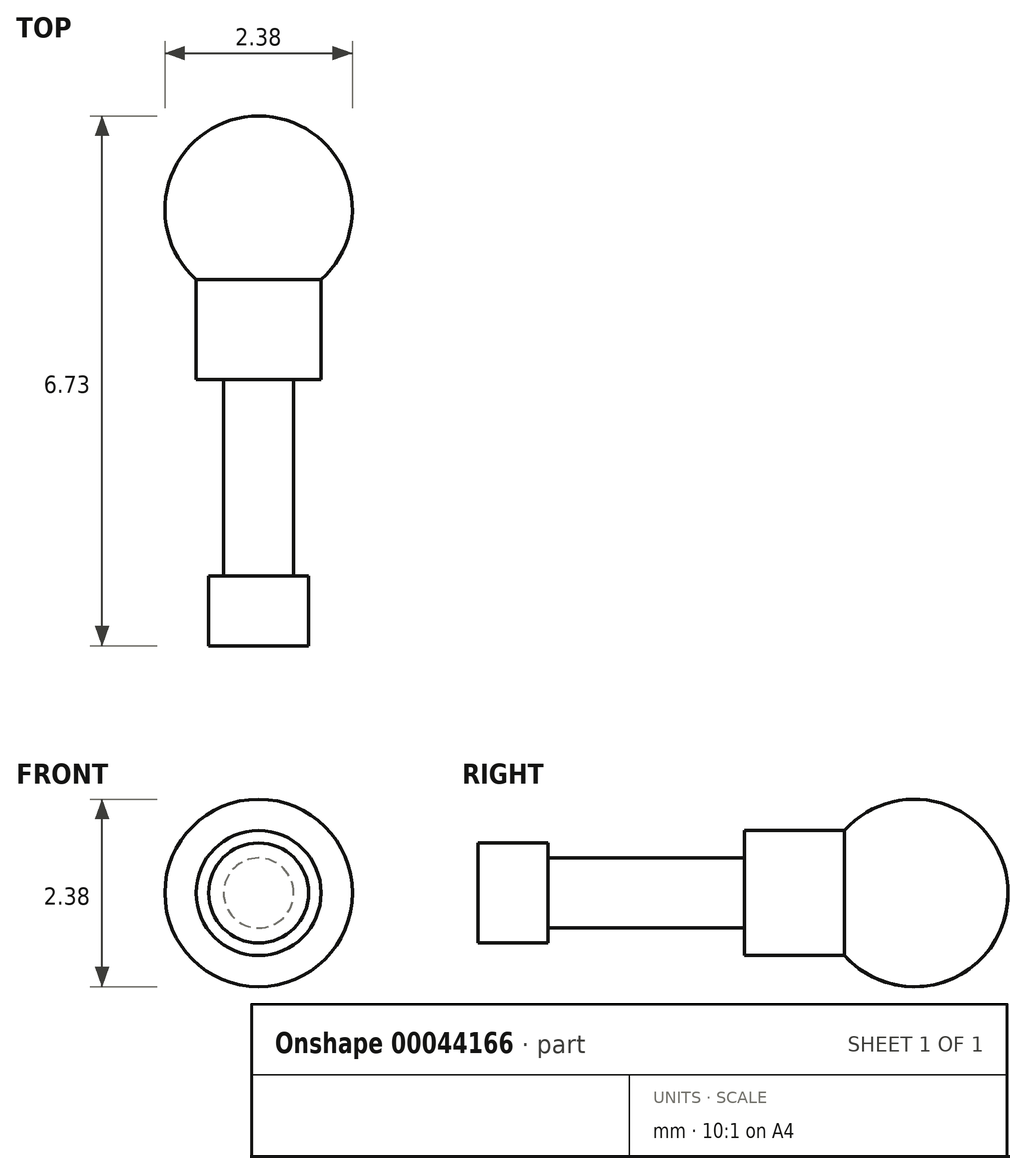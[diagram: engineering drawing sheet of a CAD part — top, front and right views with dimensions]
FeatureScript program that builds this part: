
annotation { "Feature Type Name" : "Feature", "Feature Type Description" : "" }
export const myFeature = defineFeature(function(context is Context, id is Id, definition is map)
    precondition{}
    {
        {
            var Q0;
            Q0=qCreatedBy(makeId("Right.planeOp"),FACE);
            var sketch = newSketch(context, id + "F0", { "sketchPlane" : qUnion([Q0])});
            skLineSegment(sketch, "E0", {"start": v(0, 0) * mm, "end": v(0, 0.63) * mm});
            skLineSegment(sketch, "E1", {"start": v(0, 0.63) * mm, "end": v(0.89, 0.63) * mm});
            skLineSegment(sketch, "E2", {"start": v(0.89, 0.63) * mm, "end": v(0.89, 0.44) * mm});
            skLineSegment(sketch, "E3", {"start": v(0.89, 0.44) * mm, "end": v(3.38, 0.44) * mm});
            skLineSegment(sketch, "E4", {"start": v(3.38, 0.44) * mm, "end": v(3.38, 0.8) * mm});
            skLineSegment(sketch, "E5", {"start": v(3.38, 0.8) * mm, "end": v(4.65, 0.8) * mm});
            skLineSegment(sketch, "E6", {"start": v(0, 0) * mm, "end": v(6.73, 0) * mm});
            skArc(sketch, "E7", {"start": v(6.73, 0) * mm, "mid": v(5.97, 1.11) * mm, "end": v(4.65, 0.8) * mm});
            skSolve(sketch);
        }
        {
            var Q0;
            Q0=makeQuery(id+"F0.imprint","IMPRINT",FACE,{"disambiguationData":[TD([[makeQuery(id+"F0.imprint","IMPRINT",EDGE,{"derivedFrom":sQuery(id+"F0.wireOp",EDGE,"E0")}),-1.0]])]});
            var Q1;
            Q1=sQuery(id+"F0.wireOp",EDGE,"E6");
            revolve(context, id + "F1", {"entities" : qUnion([Q0]), "axis" : qUnion([Q1]), "revolveType" : RevolveType.FULL});
        }
    });
